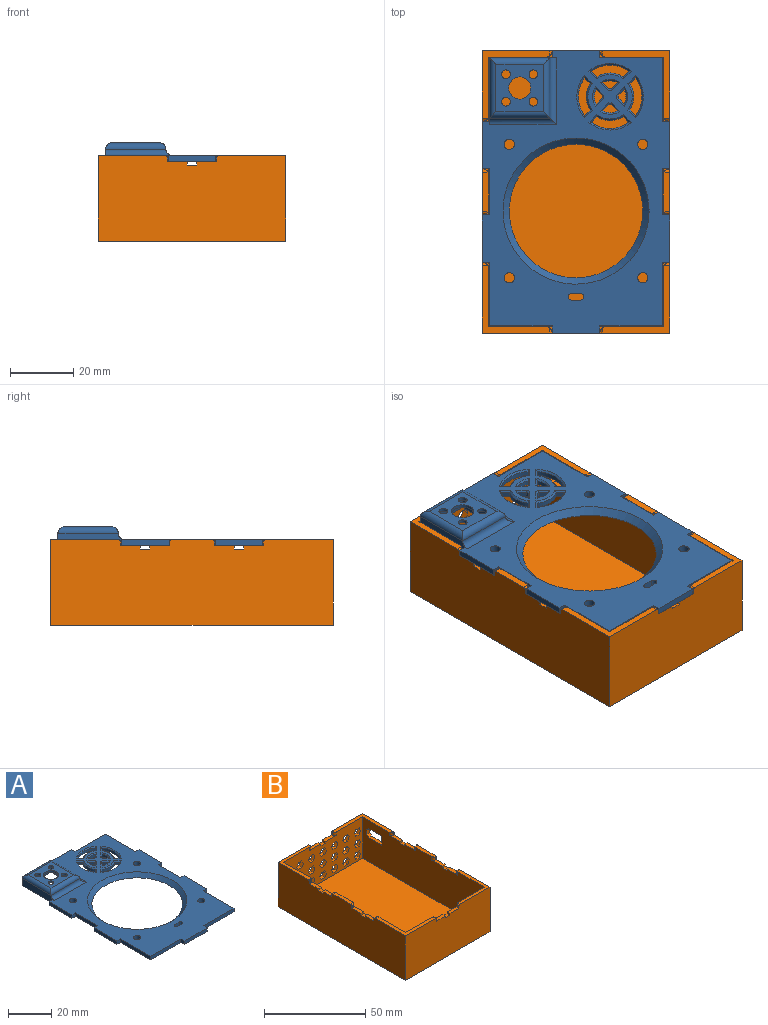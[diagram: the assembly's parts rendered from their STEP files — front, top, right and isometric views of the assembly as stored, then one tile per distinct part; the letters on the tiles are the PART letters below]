
ASSEMBLY  parts=2 mates=1
PART A: 120 faces, bbox 59x89x6 mm
  f0: plane 2.25x2mm, normal (0,1,0), area 4.5mm2, adj f2,f3,f5,f10
  f1: plane 15x2mm, normal (0,1,0), area 30mm2, adj f2,f3,f9,f18
  f2: plane 89x59mm, normal (0,0,1), area 2438.9mm2, adj f0,f1,f4,f5,f6,f7,f8,f9
  f3: plane 89x59mm, normal (0,0,-1), area 3015mm2, adj f0,f1,f4,f5,f6,f7,f8,f9
  f4: plane 15x2mm, normal (-1,0,0), area 30mm2, adj f2,f3,f21,f29
  f5: plane 15x2mm, normal (-1,0,0), area 30mm2, adj f0,f2,f3,f28
  f6: plane 15x2mm, normal (0,-1,0), area 30mm2, adj f2,f3,f22,f26
  f7: plane 15x2mm, normal (1,0,0), area 30mm2, adj f2,f3,f12,f17
  f8: plane 15x2mm, normal (1,0,0), area 30mm2, adj f2,f3,f14,f23
  f9: plane 2.25x2mm, normal (-1,0,0), area 4.5mm2, adj f1,f2,f3,f11
  f10: plane 21x4mm, normal (-1,0,0), area 78.9mm2, adj f0,f2,f3,f11,f81,f85
  f11: plane 21x4mm, normal (0,1,0), area 78.4mm2, adj f2,f3,f9,f10,f82,f86
  f12: plane 2.25x2mm, normal (0,-1,0), area 4.5mm2, adj f2,f3,f7,f13
  f13: plane 14.5x2mm, normal (1,0,0), area 29mm2, adj f2,f3,f12,f14
  f14: plane 2.25x2mm, normal (0,1,0), area 4.5mm2, adj f2,f3,f8,f13
  f15: plane 19.75x2mm, normal (0,1,0), area 39.5mm2, adj f2,f3,f16,f18
  f16: plane 20x2mm, normal (1,0,0), area 40mm2, adj f2,f3,f15,f17
  f17: plane 2.25x2mm, normal (0,1,0), area 4.5mm2, adj f2,f3,f7,f16
  f18: plane 2.25x2mm, normal (1,0,0), area 4.5mm2, adj f1,f2,f3,f15
  f19: plane 19.75x2mm, normal (0,-1,0), area 39.5mm2, adj f2,f3,f20,f22
  f20: plane 20x2mm, normal (-1,0,0), area 40mm2, adj f2,f3,f19,f21
  f21: plane 2.25x2mm, normal (0,-1,0), area 4.5mm2, adj f2,f3,f4,f20
  f22: plane 2.25x2mm, normal (-1,0,0), area 4.5mm2, adj f2,f3,f6,f19
  f23: plane 2.25x2mm, normal (0,-1,0), area 4.5mm2, adj f2,f3,f8,f24
  f24: plane 20x2mm, normal (1,0,0), area 40mm2, adj f2,f3,f23,f25
  f25: plane 19.75x2mm, normal (0,-1,0), area 39.5mm2, adj f2,f3,f24,f26
  f26: plane 2.25x2mm, normal (1,0,0), area 4.5mm2, adj f2,f3,f6,f25
  f27: plane 14.5x2mm, normal (-1,0,0), area 29mm2, adj f2,f3,f28,f29
  f28: plane 2.25x2mm, normal (0,-1,0), area 4.5mm2, adj f2,f3,f5,f27
  f29: plane 2.25x2mm, normal (0,1,0), area 4.5mm2, adj f2,f3,f4,f27
  f30: plane 15x15mm, normal (0,0,1), area 162.8mm2, adj f36,f37,f38,f39,f40,f81,f82,f83
  f31: plane 15x15mm, normal (0,0,-1), area 162.8mm2, adj f32,f33,f34,f35,f36,f37,f38,f39
  f32: plane 15x5mm, normal (0,-1,0), area 75mm2, adj f3,f31,f33,f35
  f33: plane 15x5mm, normal (-1,0,0), area 75mm2, adj f3,f31,f32,f34
  f34: plane 15x5mm, normal (0,1,0), area 75mm2, adj f3,f31,f33,f35
  f35: plane 15x5mm, normal (1,0,0), area 75mm2, adj f3,f31,f32,f34
  f36: cylinder r=1.38mm len=2.75mm, axis (0,0,1), area 8.6mm2, adj f30,f31
  f37: cylinder r=1.38mm len=2.75mm, axis (0,0,1), area 8.6mm2, adj f30,f31
  f38: cylinder r=1.38mm len=2.75mm, axis (0,0,1), area 8.6mm2, adj f30,f31
  f39: cylinder r=1.38mm len=2.75mm, axis (0,0,1), area 8.6mm2, adj f30,f31
  f40: cylinder r=3.5mm len=7mm, axis (0,0,1), area 22mm2, adj f30,f31
  f41: cylinder r=1.62mm len=3.25mm, axis (0,0,1), area 20.4mm2, adj f2,f3
  f42: plane 3x2mm, normal (0,1,0), area 6mm2, adj f2,f3,f43,f44
  f43: cylinder r=1mm len=2mm, axis (0,0,1), area 6.3mm2, adj f2,f3,f42,f45
  f44: cylinder r=1mm len=2mm, axis (0,0,1), area 6.3mm2, adj f2,f3,f42,f45
  f45: plane 3x2mm, normal (0,-1,0), area 6mm2, adj f2,f3,f43,f44
  f46: plane 1.96x1.96mm, normal (0.71,-0.71,0), area 4.2mm2, adj f3,f47,f49,f93
  f47: cylinder r=2.5mm len=1.5mm, axis (0,0,1), area 1.1mm2, adj f3,f46,f48,f94
  f48: plane 1.96x1.96mm, normal (0.71,0.71,0), area 4.2mm2, adj f3,f47,f49,f92
  f49: cylinder r=5mm len=4.62mm, axis (0,0,1), area 7.2mm2, adj f3,f46,f48,f91
  f50: cylinder r=10mm len=11.86mm, axis (0,0,1), area 19mm2, adj f3,f51,f52,f104
  f51: plane 1.8x1.8mm, normal (0.71,0.71,0), area 3.8mm2, adj f3,f50,f53,f106
  f52: plane 1.8x1.8mm, normal (0.71,-0.71,0), area 3.8mm2, adj f3,f50,f53,f103
  f53: cylinder r=7.5mm len=8.27mm, axis (0,0,1), area 13.1mm2, adj f3,f51,f52,f105
  f54: plane 1.96x1.96mm, normal (-0.71,0.71,0), area 4.2mm2, adj f3,f55,f56,f88
  f55: cylinder r=2.5mm len=1.5mm, axis (0,0,1), area 1.1mm2, adj f3,f54,f57,f90
  f56: cylinder r=5mm len=4.62mm, axis (0,0,1), area 7.2mm2, adj f3,f54,f57,f87
  f57: plane 1.96x1.96mm, normal (0.71,0.71,0), area 4.2mm2, adj f3,f55,f56,f89
  f58: plane 1.8x1.8mm, normal (0.71,0.71,0), area 3.8mm2, adj f3,f59,f61,f115
  f59: cylinder r=7.5mm len=8.27mm, axis (0,0,1), area 13.1mm2, adj f3,f58,f60,f116
  f60: plane 1.8x1.8mm, normal (-0.71,0.71,0), area 3.8mm2, adj f3,f59,f61,f118
  f61: cylinder r=10mm len=11.86mm, axis (0,0,1), area 19mm2, adj f3,f58,f60,f117
  f62: cylinder r=10mm len=11.86mm, axis (0,0,1), area 19mm2, adj f3,f63,f65,f112
  f63: plane 1.8x1.8mm, normal (-0.71,0.71,0), area 3.8mm2, adj f3,f62,f64,f114
  f64: cylinder r=7.5mm len=8.27mm, axis (0,0,1), area 13.1mm2, adj f3,f63,f65,f113
  f65: plane 1.8x1.8mm, normal (-0.71,-0.71,0), area 3.8mm2, adj f3,f62,f64,f111
  f66: cylinder r=2.5mm len=1.5mm, axis (0,0,1), area 1.1mm2, adj f3,f67,f69,f102
  f67: plane 1.96x1.96mm, normal (-0.71,-0.71,0), area 4.2mm2, adj f3,f66,f68,f100
  f68: cylinder r=5mm len=4.62mm, axis (0,0,1), area 7.2mm2, adj f3,f67,f69,f99
  f69: plane 1.96x1.96mm, normal (-0.71,0.71,0), area 4.2mm2, adj f3,f66,f68,f101
  f70: plane 1.96x1.96mm, normal (-0.71,-0.71,0), area 4.2mm2, adj f3,f71,f72,f97
  f71: cylinder r=5mm len=4.62mm, axis (0,0,1), area 7.2mm2, adj f3,f70,f73,f95
  f72: cylinder r=2.5mm len=1.5mm, axis (0,0,1), area 1.1mm2, adj f3,f70,f73,f98
  f73: plane 1.96x1.96mm, normal (0.71,-0.71,0), area 4.2mm2, adj f3,f71,f72,f96
  f74: plane 1.8x1.8mm, normal (-0.71,-0.71,0), area 3.8mm2, adj f3,f75,f76,f110
  f75: cylinder r=10mm len=11.86mm, axis (0,0,1), area 19mm2, adj f3,f74,f77,f108
  f76: cylinder r=7.5mm len=8.27mm, axis (0,0,1), area 13.1mm2, adj f3,f74,f77,f109
  f77: plane 1.8x1.8mm, normal (0.71,-0.71,0), area 3.8mm2, adj f3,f75,f76,f107
  f78: cylinder r=1.62mm len=3.25mm, axis (0,0,1), area 20.4mm2, adj f2,f3
  f79: cylinder r=1.62mm len=3.25mm, axis (0,0,1), area 20.4mm2, adj f2,f3
  f80: cylinder r=1.62mm len=3.25mm, axis (0,0,1), area 20.4mm2, adj f2,f3
  f81: cylinder r=2mm len=19mm, axis (0,-1,0), area 55.1mm2, adj f10,f30,f82,f83
  f82: cylinder r=2mm len=19mm, axis (-1,0,0), area 55.1mm2, adj f11,f30,f81,f84
  f83: cylinder r=2mm len=19mm, axis (-1,0,0), area 55.1mm2, adj f30,f81,f84,f85
  f84: cylinder r=2mm len=19mm, axis (0,-1,0), area 55.1mm2, adj f30,f82,f83,f86
  f85: cylinder r=2mm len=21mm, axis (1,0,0), area 62mm2, adj f2,f10,f83,f86
  f86: cylinder r=2mm len=21mm, axis (0,1,0), area 62mm2, adj f2,f11,f84,f85
  f87: cone r=5mm half-angle=45deg, axis (0,0,1), area 4mm2, adj f2,f56,f88,f89
  f88: plane 2.76x2.6mm, normal (-0.5,0.5,0.71), area 2.3mm2, adj f2,f54,f87,f90
  f89: plane 2.76x2.6mm, normal (0.5,0.5,0.71), area 2.3mm2, adj f2,f57,f87,f90
  f90: cone r=2mm half-angle=45deg, axis (0,0,-1), area 0.6mm2, adj f2,f55,f88,f89
  f91: cone r=5mm half-angle=45deg, axis (0,0,1), area 4mm2, adj f2,f49,f92,f93
  f92: plane 2.76x2.6mm, normal (0.5,0.5,0.71), area 2.3mm2, adj f2,f48,f91,f94
  f93: plane 2.76x2.6mm, normal (0.5,-0.5,0.71), area 2.3mm2, adj f2,f46,f91,f94
  f94: cone r=2mm half-angle=45deg, axis (0,0,-1), area 0.6mm2, adj f2,f47,f92,f93
  f95: cone r=5mm half-angle=45deg, axis (0,0,1), area 4mm2, adj f2,f71,f96,f97
  f96: plane 2.76x2.6mm, normal (0.5,-0.5,0.71), area 2.3mm2, adj f2,f73,f95,f98
  f97: plane 2.76x2.6mm, normal (-0.5,-0.5,0.71), area 2.3mm2, adj f2,f70,f95,f98
  f98: cone r=2mm half-angle=45deg, axis (0,0,-1), area 0.6mm2, adj f2,f72,f96,f97
  f99: cone r=5mm half-angle=45deg, axis (0,0,1), area 4mm2, adj f2,f68,f100,f101
  f100: plane 2.76x2.6mm, normal (-0.5,-0.5,0.71), area 2.3mm2, adj f2,f67,f99,f102
  f101: plane 2.76x2.6mm, normal (-0.5,0.5,0.71), area 2.3mm2, adj f2,f69,f99,f102
  f102: cone r=2mm half-angle=45deg, axis (0,0,-1), area 0.6mm2, adj f2,f66,f100,f101
  f103: plane 2.56x2.5mm, normal (0.5,-0.5,0.71), area 2.1mm2, adj f2,f52,f104,f105
  f104: cone r=10mm half-angle=45deg, axis (0,0,1), area 9.6mm2, adj f2,f50,f103,f106
  f105: cone r=7mm half-angle=45deg, axis (0,0,-1), area 6.3mm2, adj f2,f53,f103,f106
  f106: plane 2.56x2.5mm, normal (0.5,0.5,0.71), area 2.1mm2, adj f2,f51,f104,f105
  f107: plane 2.56x2.5mm, normal (0.5,-0.5,0.71), area 2.1mm2, adj f2,f77,f108,f109
  f108: cone r=10mm half-angle=45deg, axis (0,0,1), area 9.6mm2, adj f2,f75,f107,f110
  f109: cone r=7mm half-angle=45deg, axis (0,0,-1), area 6.3mm2, adj f2,f76,f107,f110
  f110: plane 2.56x2.5mm, normal (-0.5,-0.5,0.71), area 2.1mm2, adj f2,f74,f108,f109
  f111: plane 2.56x2.5mm, normal (-0.5,-0.5,0.71), area 2.1mm2, adj f2,f65,f112,f113
  f112: cone r=10mm half-angle=45deg, axis (0,0,1), area 9.6mm2, adj f2,f62,f111,f114
  f113: cone r=7mm half-angle=45deg, axis (0,0,-1), area 6.3mm2, adj f2,f64,f111,f114
  f114: plane 2.56x2.5mm, normal (-0.5,0.5,0.71), area 2.1mm2, adj f2,f63,f112,f113
  f115: plane 2.56x2.5mm, normal (0.5,0.5,0.71), area 2.1mm2, adj f2,f58,f116,f117
  f116: cone r=7mm half-angle=45deg, axis (0,0,-1), area 6.3mm2, adj f2,f59,f115,f118
  f117: cone r=10mm half-angle=45deg, axis (0,0,1), area 9.6mm2, adj f2,f61,f115,f118
  f118: plane 2.56x2.5mm, normal (-0.5,0.5,0.71), area 2.1mm2, adj f2,f60,f116,f117
  f119: cone r=21.04mm half-angle=45deg, axis (0,0,1), area 391.6mm2, adj f2,f3
PART B: 214 faces, bbox 59x89x27 mm
  f0: plane 7.75x2mm, normal (0,0,1), area 13mm2, adj f8,f17,f22,f57,f209
  f1: plane 7.75x2mm, normal (0,0,1), area 13mm2, adj f8,f17,f25,f55,f206
  f2: plane 7.75x2mm, normal (0,0,1), area 13mm2, adj f7,f18,f29,f58,f202
  f3: plane 7.75x2mm, normal (0,0,1), area 13mm2, adj f6,f19,f32,f62,f199
  f4: plane 7.75x2mm, normal (0,0,1), area 13mm2, adj f6,f19,f35,f61,f196
  f5: plane 7.75x2mm, normal (0,0,1), area 13mm2, adj f9,f10,f37,f53,f212
  f6: plane 85x25mm, normal (1,0,0), area 2045mm2, adj f3,f4,f9,f11,f15,f18,f20,f21
  f7: plane 59x27mm, normal (0,-1,0), area 1558.8mm2, adj f2,f8,f14,f15,f16,f19,f28,f29
  f8: plane 89x27mm, normal (1,0,0), area 2280.4mm2, adj f0,f1,f7,f10,f12,f13,f14,f16
  f9: plane 55x25mm, normal (0,-1,0), area 1044mm2, adj f5,f6,f11,f13,f17,f21,f39,f52
  f10: plane 59x27mm, normal (0,1,0), area 1267.8mm2, adj f5,f8,f11,f13,f16,f19,f37,f38
  f11: plane 21.25x21mm, normal (0,0,1), area 80.4mm2, adj f6,f9,f10,f19,f41,f51,f53,f62
  f12: plane 12.5x2mm, normal (0,0,1), area 24.9mm2, adj f8,f17,f43,f45,f54,f57
  f13: plane 21.25x21mm, normal (0,0,1), area 80.4mm2, adj f8,f9,f10,f17,f40,f42,f52,f55
  f14: plane 21.25x21mm, normal (0,0,1), area 80.4mm2, adj f7,f8,f17,f18,f44,f47,f56,f58
  f15: plane 21.25x21mm, normal (0,0,1), area 80.4mm2, adj f6,f7,f18,f19,f46,f48,f59,f60
  f16: plane 89x59mm, normal (0,0,-1), area 5251mm2, adj f7,f8,f10,f19
  f17: plane 85x25mm, normal (-1,0,0), area 1990.8mm2, adj f0,f1,f9,f12,f13,f14,f18,f21
  f18: plane 55x25mm, normal (0,1,0), area 1335mm2, adj f2,f6,f14,f15,f17,f21,f30,f58
  f19: plane 89x27mm, normal (-1,0,0), area 2334.5mm2, adj f3,f4,f7,f10,f11,f15,f16,f20
  f20: plane 12.5x2mm, normal (0,0,1), area 24.9mm2, adj f6,f19,f49,f50,f61,f63
  f21: plane 85x55mm, normal (0,0,1), area 4675mm2, adj f6,f9,f17,f18
  f22: plane 1.25x0.5mm, normal (0,-1,0), area 0.6mm2, adj f0,f8,f45,f57
  f23: plane 1.25x0.5mm, normal (0,1,0), area 0.6mm2, adj f8,f24,f44,f56
  f24: plane 7.75x2mm, normal (0,0,1), area 13mm2, adj f8,f17,f23,f56,f208
  f25: plane 1.25x0.5mm, normal (0,-1,0), area 0.6mm2, adj f1,f8,f42,f55
  f26: plane 1.25x0.5mm, normal (0,1,0), area 0.6mm2, adj f8,f27,f43,f54
  f27: plane 7.75x2mm, normal (0,0,1), area 13mm2, adj f8,f17,f26,f54,f205
  f28: plane 1.25x0.5mm, normal (1,0,0), area 0.6mm2, adj f7,f30,f46,f59
  f29: plane 1.25x0.5mm, normal (-1,0,0), area 0.6mm2, adj f2,f7,f47,f58
  f30: plane 7.75x2mm, normal (0,0,1), area 13mm2, adj f7,f18,f28,f59,f203
  f31: plane 1.25x0.5mm, normal (0,1,0), area 0.6mm2, adj f19,f33,f50,f63
  f32: plane 1.25x0.5mm, normal (0,-1,0), area 0.6mm2, adj f3,f19,f51,f62
  f33: plane 7.75x2mm, normal (0,0,1), area 13mm2, adj f6,f19,f31,f63,f200
  f34: plane 1.25x0.5mm, normal (0,1,0), area 0.6mm2, adj f19,f36,f48,f60
  f35: plane 1.25x0.5mm, normal (0,-1,0), area 0.6mm2, adj f4,f19,f49,f61
  f36: plane 7.75x2mm, normal (0,0,1), area 13mm2, adj f6,f19,f34,f60,f197
  f37: plane 1.25x0.5mm, normal (1,0,0), area 0.6mm2, adj f5,f10,f41,f53
  f38: plane 1.25x0.5mm, normal (-1,0,0), area 0.6mm2, adj f10,f39,f40,f52
  f39: plane 7.75x2mm, normal (0,0,1), area 13mm2, adj f9,f10,f38,f52,f211
  f40: cylinder r=0.75mm len=1.8mm, axis (0,-1,0), area 1.5mm2, adj f10,f13,f38,f52
  f41: cylinder r=0.75mm len=1.8mm, axis (0,1,0), area 1.5mm2, adj f10,f11,f37,f53
  f42: cylinder r=0.75mm len=1.8mm, axis (1,0,0), area 1.5mm2, adj f8,f13,f25,f55
  f43: cylinder r=0.75mm len=1.8mm, axis (-1,0,0), area 1.5mm2, adj f8,f12,f26,f54
  f44: cylinder r=0.75mm len=1.8mm, axis (-1,0,0), area 1.5mm2, adj f8,f14,f23,f56
  f45: cylinder r=0.75mm len=1.8mm, axis (1,0,0), area 1.5mm2, adj f8,f12,f22,f57
  f46: cylinder r=0.75mm len=1.8mm, axis (0,1,0), area 1.5mm2, adj f7,f15,f28,f59
  f47: cylinder r=0.75mm len=1.8mm, axis (0,-1,0), area 1.5mm2, adj f7,f14,f29,f58
  f48: cylinder r=0.75mm len=1.8mm, axis (-1,0,0), area 1.5mm2, adj f15,f19,f34,f60
  f49: cylinder r=0.75mm len=1.8mm, axis (1,0,0), area 1.5mm2, adj f19,f20,f35,f61
  f50: cylinder r=0.75mm len=1.8mm, axis (-1,0,0), area 1.5mm2, adj f19,f20,f31,f63
  f51: cylinder r=0.75mm len=1.8mm, axis (1,0,0), area 1.5mm2, adj f11,f19,f32,f62
  f52: cylinder r=1.5mm len=2mm, axis (0,0,-1), area 4.3mm2, adj f9,f13,f38,f39,f40
  f53: cylinder r=1.5mm len=2mm, axis (0,0,1), area 4.3mm2, adj f5,f9,f11,f37,f41
  f54: cylinder r=1.5mm len=2mm, axis (0,0,-1), area 4.3mm2, adj f12,f17,f26,f27,f43
  f55: cylinder r=1.5mm len=2mm, axis (0,0,1), area 4.3mm2, adj f1,f13,f17,f25,f42
  f56: cylinder r=1.5mm len=2mm, axis (0,0,-1), area 4.3mm2, adj f14,f17,f23,f24,f44
  f57: cylinder r=1.5mm len=2mm, axis (0,0,-1), area 4.3mm2, adj f0,f12,f17,f22,f45
  f58: cylinder r=1.5mm len=2mm, axis (0,0,-1), area 4.3mm2, adj f2,f14,f18,f29,f47
  f59: cylinder r=1.5mm len=2mm, axis (0,0,1), area 4.3mm2, adj f15,f18,f28,f30,f46
  f60: cylinder r=1.5mm len=2mm, axis (0,0,-1), area 4.3mm2, adj f6,f15,f34,f36,f48
  f61: cylinder r=1.5mm len=2mm, axis (0,0,-1), area 4.3mm2, adj f4,f6,f20,f35,f49
  f62: cylinder r=1.5mm len=2mm, axis (0,0,1), area 4.3mm2, adj f3,f6,f11,f32,f51
  f63: cylinder r=1.5mm len=2mm, axis (0,0,-1), area 4.3mm2, adj f6,f20,f31,f33,f50
  f64: plane 2x2mm, normal (0.87,0,-0.5), area 4.6mm2, adj f9,f10,f65,f69
  f65: plane 2.31x2mm, normal (0,0,-1), area 4.6mm2, adj f9,f10,f64,f66
  f66: plane 2x2mm, normal (-0.87,0,-0.5), area 4.6mm2, adj f9,f10,f65,f67
  f67: plane 2x2mm, normal (-0.87,0,0.5), area 4.6mm2, adj f9,f10,f66,f68
  f68: plane 2.31x2mm, normal (0,0,1), area 4.6mm2, adj f9,f10,f67,f69
  f69: plane 2x2mm, normal (0.87,0,0.5), area 4.6mm2, adj f9,f10,f64,f68
  f70: plane 2.31x2mm, normal (0,0,1), area 4.6mm2, adj f9,f10,f71,f75
  f71: plane 2x2mm, normal (0.87,0,0.5), area 4.6mm2, adj f9,f10,f70,f72
  f72: plane 2x2mm, normal (0.87,0,-0.5), area 4.6mm2, adj f9,f10,f71,f73
  f73: plane 2.31x2mm, normal (0,0,-1), area 4.6mm2, adj f9,f10,f72,f74
  f74: plane 2x2mm, normal (-0.87,0,-0.5), area 4.6mm2, adj f9,f10,f73,f75
  f75: plane 2x2mm, normal (-0.87,0,0.5), area 4.6mm2, adj f9,f10,f70,f74
  f76: plane 2x2mm, normal (-0.87,0,0.5), area 4.6mm2, adj f9,f10,f77,f81
  f77: plane 2.31x2mm, normal (0,0,1), area 4.6mm2, adj f9,f10,f76,f78
  f78: plane 2x2mm, normal (0.87,0,0.5), area 4.6mm2, adj f9,f10,f77,f79
  f79: plane 2x2mm, normal (0.87,0,-0.5), area 4.6mm2, adj f9,f10,f78,f80
  f80: plane 2.31x2mm, normal (0,0,-1), area 4.6mm2, adj f9,f10,f79,f81
  f81: plane 2x2mm, normal (-0.87,0,-0.5), area 4.6mm2, adj f9,f10,f76,f80
  f82: plane 2x2mm, normal (-0.87,0,0.5), area 4.6mm2, adj f9,f10,f83,f87
  f83: plane 2.31x2mm, normal (0,0,1), area 4.6mm2, adj f9,f10,f82,f84
  f84: plane 2x2mm, normal (0.87,0,0.5), area 4.6mm2, adj f9,f10,f83,f85
  f85: plane 2x2mm, normal (0.87,0,-0.5), area 4.6mm2, adj f9,f10,f84,f86
  f86: plane 2.31x2mm, normal (0,0,-1), area 4.6mm2, adj f9,f10,f85,f87
  f87: plane 2x2mm, normal (-0.87,0,-0.5), area 4.6mm2, adj f9,f10,f82,f86
  f88: plane 2.31x2mm, normal (0,0,-1), area 4.6mm2, adj f9,f10,f89,f93
  f89: plane 2x2mm, normal (-0.87,0,-0.5), area 4.6mm2, adj f9,f10,f88,f90
  f90: plane 2x2mm, normal (-0.87,0,0.5), area 4.6mm2, adj f9,f10,f89,f91
  f91: plane 2.31x2mm, normal (0,0,1), area 4.6mm2, adj f9,f10,f90,f92
  f92: plane 2x2mm, normal (0.87,0,0.5), area 4.6mm2, adj f9,f10,f91,f93
  f93: plane 2x2mm, normal (0.87,0,-0.5), area 4.6mm2, adj f9,f10,f88,f92
  f94: plane 2x2mm, normal (0.87,0,0.5), area 4.6mm2, adj f9,f10,f95,f99
  f95: plane 2x2mm, normal (0.87,0,-0.5), area 4.6mm2, adj f9,f10,f94,f96
  f96: plane 2.31x2mm, normal (0,0,-1), area 4.6mm2, adj f9,f10,f95,f97
  f97: plane 2x2mm, normal (-0.87,0,-0.5), area 4.6mm2, adj f9,f10,f96,f98
  f98: plane 2x2mm, normal (-0.87,0,0.5), area 4.6mm2, adj f9,f10,f97,f99
  f99: plane 2.31x2mm, normal (0,0,1), area 4.6mm2, adj f9,f10,f94,f98
  f100: plane 2.31x2mm, normal (0,0,1), area 4.6mm2, adj f9,f10,f101,f105
  f101: plane 2x2mm, normal (0.87,0,0.5), area 4.6mm2, adj f9,f10,f100,f102
  f102: plane 2x2mm, normal (0.87,0,-0.5), area 4.6mm2, adj f9,f10,f101,f103
  f103: plane 2.31x2mm, normal (0,0,-1), area 4.6mm2, adj f9,f10,f102,f104
  f104: plane 2x2mm, normal (-0.87,0,-0.5), area 4.6mm2, adj f9,f10,f103,f105
  f105: plane 2x2mm, normal (-0.87,0,0.5), area 4.6mm2, adj f9,f10,f100,f104
  f106: plane 2.31x2mm, normal (0,0,-1), area 4.6mm2, adj f9,f10,f107,f109
  f107: plane 2x2mm, normal (-0.87,0,-0.5), area 4.6mm2, adj f9,f10,f106,f108
  f108: plane 2x2mm, normal (-0.87,0,0.5), area 4.6mm2, adj f9,f10,f107,f110
  f109: plane 2x2mm, normal (0.87,0,-0.5), area 4.6mm2, adj f9,f10,f106,f111
  f110: plane 2.31x2mm, normal (0,0,1), area 4.6mm2, adj f9,f10,f108,f111
  f111: plane 2x2mm, normal (0.87,0,0.5), area 4.6mm2, adj f9,f10,f109,f110
  f112: plane 2.31x2mm, normal (0,0,-1), area 4.6mm2, adj f9,f10,f113,f115
  f113: plane 2x2mm, normal (-0.87,0,-0.5), area 4.6mm2, adj f9,f10,f112,f114
  f114: plane 2x2mm, normal (-0.87,0,0.5), area 4.6mm2, adj f9,f10,f113,f116
  f115: plane 2x2mm, normal (0.87,0,-0.5), area 4.6mm2, adj f9,f10,f112,f117
  f116: plane 2.31x2mm, normal (0,0,1), area 4.6mm2, adj f9,f10,f114,f117
  f117: plane 2x2mm, normal (0.87,0,0.5), area 4.6mm2, adj f9,f10,f115,f116
  f118: plane 2.31x2mm, normal (0,0,-1), area 4.6mm2, adj f9,f10,f119,f121
  f119: plane 2x2mm, normal (-0.87,0,-0.5), area 4.6mm2, adj f9,f10,f118,f120
  f120: plane 2x2mm, normal (-0.87,0,0.5), area 4.6mm2, adj f9,f10,f119,f122
  f121: plane 2x2mm, normal (0.87,0,-0.5), area 4.6mm2, adj f9,f10,f118,f123
  f122: plane 2.31x2mm, normal (0,0,1), area 4.6mm2, adj f9,f10,f120,f123
  f123: plane 2x2mm, normal (0.87,0,0.5), area 4.6mm2, adj f9,f10,f121,f122
  f124: plane 2.31x2mm, normal (0,0,-1), area 4.6mm2, adj f9,f10,f125,f127
  f125: plane 2x2mm, normal (-0.87,0,-0.5), area 4.6mm2, adj f9,f10,f124,f126
  f126: plane 2x2mm, normal (-0.87,0,0.5), area 4.6mm2, adj f9,f10,f125,f128
  f127: plane 2x2mm, normal (0.87,0,-0.5), area 4.6mm2, adj f9,f10,f124,f129
  f128: plane 2.31x2mm, normal (0,0,1), area 4.6mm2, adj f9,f10,f126,f129
  f129: plane 2x2mm, normal (0.87,0,0.5), area 4.6mm2, adj f9,f10,f127,f128
  f130: plane 2x2mm, normal (0.87,0,-0.5), area 4.6mm2, adj f9,f10,f131,f135
  f131: plane 2.31x2mm, normal (0,0,-1), area 4.6mm2, adj f9,f10,f130,f132
  f132: plane 2x2mm, normal (-0.87,0,-0.5), area 4.6mm2, adj f9,f10,f131,f133
  f133: plane 2x2mm, normal (-0.87,0,0.5), area 4.6mm2, adj f9,f10,f132,f134
  f134: plane 2.31x2mm, normal (0,0,1), area 4.6mm2, adj f9,f10,f133,f135
  f135: plane 2x2mm, normal (0.87,0,0.5), area 4.6mm2, adj f9,f10,f130,f134
  f136: plane 2x2mm, normal (0.87,0,-0.5), area 4.6mm2, adj f9,f10,f137,f141
  f137: plane 2.31x2mm, normal (0,0,-1), area 4.6mm2, adj f9,f10,f136,f138
  f138: plane 2x2mm, normal (-0.87,0,-0.5), area 4.6mm2, adj f9,f10,f137,f139
  f139: plane 2x2mm, normal (-0.87,0,0.5), area 4.6mm2, adj f9,f10,f138,f140
  f140: plane 2.31x2mm, normal (0,0,1), area 4.6mm2, adj f9,f10,f139,f141
  f141: plane 2x2mm, normal (0.87,0,0.5), area 4.6mm2, adj f9,f10,f136,f140
  f142: plane 2.31x2mm, normal (0,0,-1), area 4.6mm2, adj f9,f10,f143,f145
  f143: plane 2x2mm, normal (-0.87,0,-0.5), area 4.6mm2, adj f9,f10,f142,f144
  f144: plane 2x2mm, normal (-0.87,0,0.5), area 4.6mm2, adj f9,f10,f143,f146
  f145: plane 2x2mm, normal (0.87,0,-0.5), area 4.6mm2, adj f9,f10,f142,f147
  f146: plane 2.31x2mm, normal (0,0,1), area 4.6mm2, adj f9,f10,f144,f147
  f147: plane 2x2mm, normal (0.87,0,0.5), area 4.6mm2, adj f9,f10,f145,f146
  f148: plane 2.31x2mm, normal (0,0,-1), area 4.6mm2, adj f9,f10,f149,f151
  f149: plane 2x2mm, normal (-0.87,0,-0.5), area 4.6mm2, adj f9,f10,f148,f150
  f150: plane 2x2mm, normal (-0.87,0,0.5), area 4.6mm2, adj f9,f10,f149,f152
  f151: plane 2x2mm, normal (0.87,0,-0.5), area 4.6mm2, adj f9,f10,f148,f153
  f152: plane 2.31x2mm, normal (0,0,1), area 4.6mm2, adj f9,f10,f150,f153
  f153: plane 2x2mm, normal (0.87,0,0.5), area 4.6mm2, adj f9,f10,f151,f152
  f154: plane 2x2mm, normal (-0.87,0,-0.5), area 4.6mm2, adj f9,f10,f155,f157
  f155: plane 2x2mm, normal (-0.87,0,0.5), area 4.6mm2, adj f9,f10,f154,f156
  f156: plane 2.31x2mm, normal (0,0,1), area 4.6mm2, adj f9,f10,f155,f158
  f157: plane 2.31x2mm, normal (0,0,-1), area 4.6mm2, adj f9,f10,f154,f159
  f158: plane 2x2mm, normal (0.87,0,0.5), area 4.6mm2, adj f9,f10,f156,f159
  f159: plane 2x2mm, normal (0.87,0,-0.5), area 4.6mm2, adj f9,f10,f157,f158
  f160: plane 2x2mm, normal (-0.87,0,-0.5), area 4.6mm2, adj f9,f10,f161,f163
  f161: plane 2x2mm, normal (-0.87,0,0.5), area 4.6mm2, adj f9,f10,f160,f162
  f162: plane 2.31x2mm, normal (0,0,1), area 4.6mm2, adj f9,f10,f161,f164
  f163: plane 2.31x2mm, normal (0,0,-1), area 4.6mm2, adj f9,f10,f160,f165
  f164: plane 2x2mm, normal (0.87,0,0.5), area 4.6mm2, adj f9,f10,f162,f165
  f165: plane 2x2mm, normal (0.87,0,-0.5), area 4.6mm2, adj f9,f10,f163,f164
  f166: plane 2.31x2mm, normal (0,0,-1), area 4.6mm2, adj f9,f10,f167,f169
  f167: plane 2x2mm, normal (-0.87,0,-0.5), area 4.6mm2, adj f9,f10,f166,f168
  f168: plane 2x2mm, normal (-0.87,0,0.5), area 4.6mm2, adj f9,f10,f167,f170
  f169: plane 2x2mm, normal (0.87,0,-0.5), area 4.6mm2, adj f9,f10,f166,f171
  f170: plane 2.31x2mm, normal (0,0,1), area 4.6mm2, adj f9,f10,f168,f171
  f171: plane 2x2mm, normal (0.87,0,0.5), area 4.6mm2, adj f9,f10,f169,f170
  f172: plane 2.31x2mm, normal (0,0,-1), area 4.6mm2, adj f9,f10,f173,f175
  f173: plane 2x2mm, normal (-0.87,0,-0.5), area 4.6mm2, adj f9,f10,f172,f174
  f174: plane 2x2mm, normal (-0.87,0,0.5), area 4.6mm2, adj f9,f10,f173,f176
  f175: plane 2x2mm, normal (0.87,0,-0.5), area 4.6mm2, adj f9,f10,f172,f177
  f176: plane 2.31x2mm, normal (0,0,1), area 4.6mm2, adj f9,f10,f174,f177
  f177: plane 2x2mm, normal (0.87,0,0.5), area 4.6mm2, adj f9,f10,f175,f176
  f178: plane 2.31x2mm, normal (0,0,1), area 4.6mm2, adj f9,f10,f179,f181
  f179: plane 2x2mm, normal (0.87,0,0.5), area 4.6mm2, adj f9,f10,f178,f180
  f180: plane 2x2mm, normal (0.87,0,-0.5), area 4.6mm2, adj f9,f10,f179,f182
  f181: plane 2x2mm, normal (-0.87,0,0.5), area 4.6mm2, adj f9,f10,f178,f183
  f182: plane 2.31x2mm, normal (0,0,-1), area 4.6mm2, adj f9,f10,f180,f183
  f183: plane 2x2mm, normal (-0.87,0,-0.5), area 4.6mm2, adj f9,f10,f181,f182
  f184: plane 2x2mm, normal (0.87,0,-0.5), area 4.6mm2, adj f9,f10,f185,f189
  f185: plane 2.31x2mm, normal (0,0,-1), area 4.6mm2, adj f9,f10,f184,f186
  f186: plane 2x2mm, normal (-0.87,0,-0.5), area 4.6mm2, adj f9,f10,f185,f187
  f187: plane 2x2mm, normal (-0.87,0,0.5), area 4.6mm2, adj f9,f10,f186,f188
  f188: plane 2.31x2mm, normal (0,0,1), area 4.6mm2, adj f9,f10,f187,f189
  f189: plane 2x2mm, normal (0.87,0,0.5), area 4.6mm2, adj f9,f10,f184,f188
  f190: plane 8.99x2mm, normal (0,0,-1), area 18mm2, adj f8,f17,f191,f193
  f191: plane 5.4x2mm, normal (0,1,0), area 10.8mm2, adj f8,f17,f190,f192
  f192: plane 8.99x2mm, normal (0,0,1), area 18mm2, adj f8,f17,f191,f194
  f193: plane 2x1.41mm, normal (0,-0.71,-0.71), area 4mm2, adj f8,f17,f190,f195
  f194: plane 2x1.41mm, normal (0,-0.71,0.71), area 4mm2, adj f8,f17,f192,f195
  f195: plane 2.57x2mm, normal (0,-1,0), area 5.1mm2, adj f8,f17,f193,f194
  f196: plane 2x1mm, normal (0,-1,0), area 2mm2, adj f4,f6,f19,f198
  f197: plane 2x1mm, normal (0,1,0), area 2mm2, adj f6,f19,f36,f198
  f198: plane 3x2mm, normal (0,0,1), area 6mm2, adj f6,f19,f196,f197
  f199: plane 2x1mm, normal (0,-1,0), area 2mm2, adj f3,f6,f19,f201
  f200: plane 2x1mm, normal (0,1,0), area 2mm2, adj f6,f19,f33,f201
  f201: plane 3x2mm, normal (0,0,1), area 6mm2, adj f6,f19,f199,f200
  f202: plane 2x1mm, normal (-1,0,0), area 2mm2, adj f2,f7,f18,f204
  f203: plane 2x1mm, normal (1,0,0), area 2mm2, adj f7,f18,f30,f204
  f204: plane 3x2mm, normal (0,0,1), area 6mm2, adj f7,f18,f202,f203
  f205: plane 2x1mm, normal (0,1,0), area 2mm2, adj f8,f17,f27,f207
  f206: plane 2x1mm, normal (0,-1,0), area 2mm2, adj f1,f8,f17,f207
  f207: plane 3x2mm, normal (0,0,1), area 6mm2, adj f8,f17,f205,f206
  f208: plane 2x1mm, normal (0,1,0), area 2mm2, adj f8,f17,f24,f210
  f209: plane 2x1mm, normal (0,-1,0), area 2mm2, adj f0,f8,f17,f210
  f210: plane 3x2mm, normal (0,0,1), area 6mm2, adj f8,f17,f208,f209
  f211: plane 2x1mm, normal (-1,0,0), area 2mm2, adj f9,f10,f39,f213
  f212: plane 2x1mm, normal (1,0,0), area 2mm2, adj f5,f9,f10,f213
  f213: plane 3x2mm, normal (0,0,1), area 6mm2, adj f9,f10,f211,f212
PLACE A t=(-35,0,25)mm
PLACE B t=(35,0,0)mm
MATE slider A.f2 <-> B.f21  axis (0,0,1) through (2.07,-4.1,27)mm
